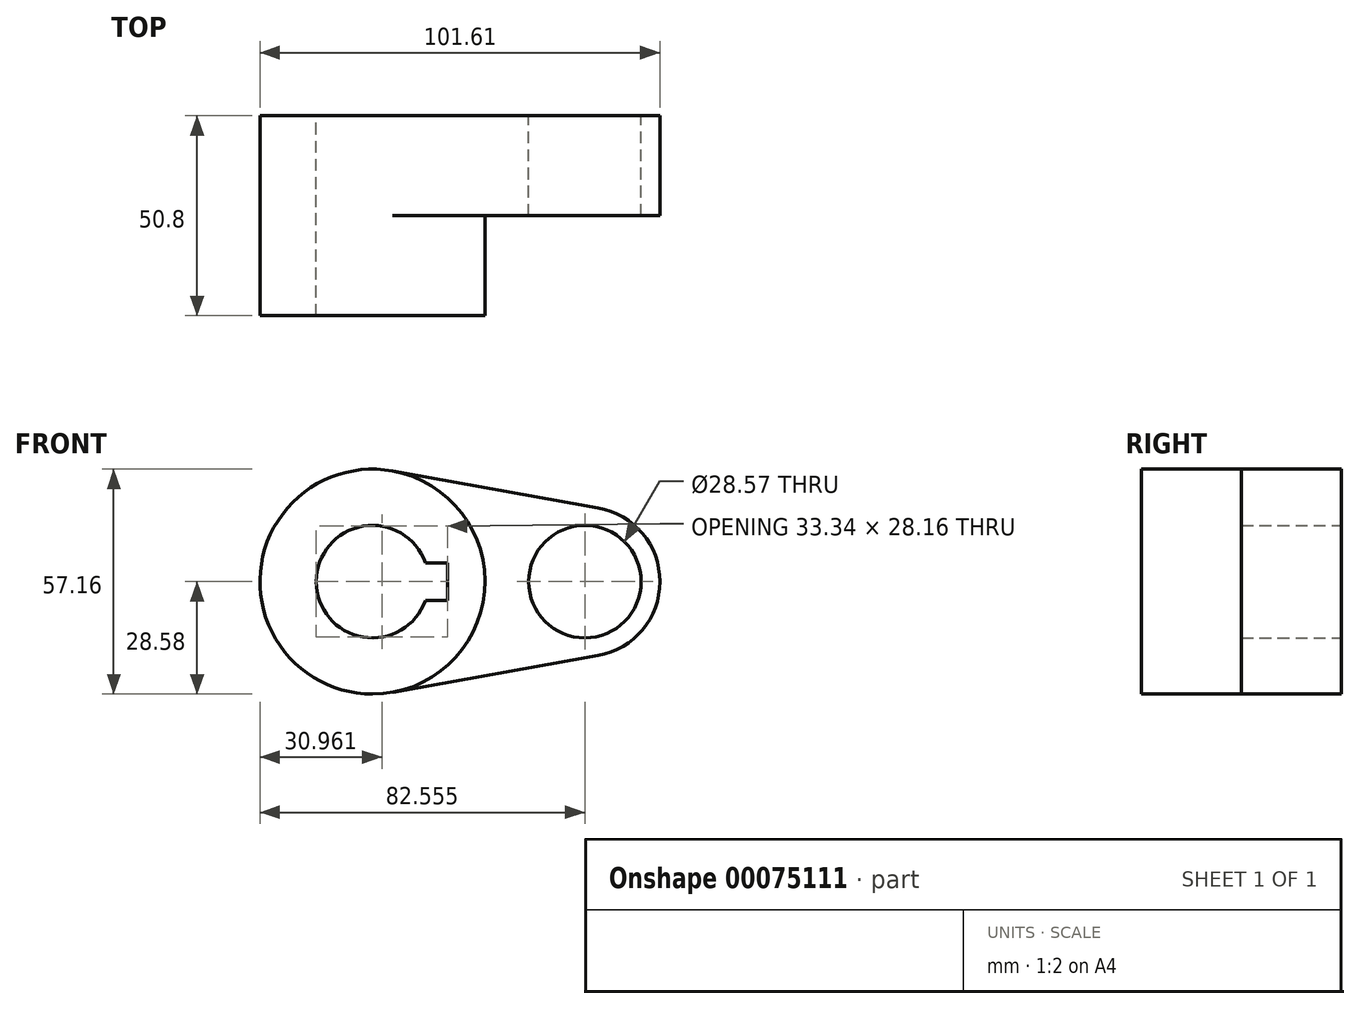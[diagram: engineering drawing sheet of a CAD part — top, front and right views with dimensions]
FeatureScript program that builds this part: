
annotation { "Feature Type Name" : "Feature", "Feature Type Description" : "" }
export const myFeature = defineFeature(function(context is Context, id is Id, definition is map)
    precondition{}
    {
        {
            var Q0;
            Q0=qCreatedBy(makeId("Front.planeOp"),FACE);
            var sketch = newSketch(context, id + "F0", { "sketchPlane" : qUnion([Q0])});
            skCircle(sketch, "E0", {"center": v(0, 0) * mm, "radius": 28.57 * mm});
            skCircle(sketch, "E1", {"center": v(53.98, 0) * mm, "radius": 19.05 * mm});
            skLineSegment(sketch, "E2", {"start": v(5.04, 28.13) * mm, "end": v(57.34, 18.75) * mm});
            skLineSegment(sketch, "E3", {"start": v(5.04, -28.13) * mm, "end": v(57.34, -18.75) * mm});
            skCircle(sketch, "E4", {"center": v(0, 0) * mm, "radius": 14.29 * mm});
            skCircle(sketch, "E5", {"center": v(53.98, 0) * mm, "radius": 14.29 * mm});
            skLineSegment(sketch, "E6.rect.bottom", {"start": v(19.05, 4.76) * mm, "end": v(-19.05, 4.76) * mm});
            skLineSegment(sketch, "E6.rect.top", {"start": v(19.05, -4.76) * mm, "end": v(-19.05, -4.76) * mm});
            skLineSegment(sketch, "E6.rect.left", {"start": v(19.05, 4.76) * mm, "end": v(19.05, -4.76) * mm});
            skLineSegment(sketch, "E6.rect.right", {"start": v(-19.05, 4.76) * mm, "end": v(-19.05, -4.76) * mm});
            skSolve(sketch);
        }
        {
            var Q0;
            {var subQ11=sQuery(id+"F0.wireOp",EDGE,"E6.rect.left");Q0=makeQuery(id+"F0.imprint","IMPRINT",FACE,{"disambiguationData":[TD([[makeQuery(id+"F0.imprint","IMPRINT",EDGE,{"derivedFrom":subQ11}),1.0]])]});}
            var Q1;
            {var subQ5=sQuery(id+"F0.wireOp",EDGE,"E6.rect.right");Q1=makeQuery(id+"F0.imprint","IMPRINT",FACE,{"disambiguationData":[TD([[makeQuery(id+"F0.imprint","IMPRINT",EDGE,{"derivedFrom":subQ5}),1.0]])]});}
            var Q2;
            Q2=makeQuery(id+"F0.imprint","IMPRINT",FACE,{"disambiguationData":[TD([[makeQuery(id+"F0.imprint","IMPRINT",EDGE,{"derivedFrom":sQuery(id+"F0.wireOp",EDGE,"E5")}),-1.0]])]});
            var Q3;
            {var subQ0=sQuery(id+"F0.wireOp",EDGE,"E2");Q3=makeQuery(id+"F0.imprint","IMPRINT",FACE,{"disambiguationData":[TD([[makeQuery(id+"F0.imprint","IMPRINT",EDGE,{"derivedFrom":subQ0}),-1.0]])]});}
            extrude(context, id + "F1", {"entities" : qUnion([Q0, Q1, Q2, Q3]), "depth" : 25.4 * mm});
        }
        {
            var Q0;
            {var subQ11=sQuery(id+"F0.wireOp",EDGE,"E6.rect.left");Q0=makeQuery(id+"F0.imprint","IMPRINT",FACE,{"disambiguationData":[TD([[makeQuery(id+"F0.imprint","IMPRINT",EDGE,{"derivedFrom":subQ11}),1.0]])]});}
            var Q1;
            {var subQ5=sQuery(id+"F0.wireOp",EDGE,"E6.rect.right");Q1=makeQuery(id+"F0.imprint","IMPRINT",FACE,{"disambiguationData":[TD([[makeQuery(id+"F0.imprint","IMPRINT",EDGE,{"derivedFrom":subQ5}),1.0]])]});}
            extrude(context, id + "F2", {"entities" : qUnion([Q0, Q1]), "operationType" : NewBodyOperationType.ADD, "depth" : 50.8 * mm});
        }
    });
